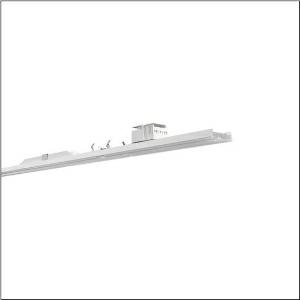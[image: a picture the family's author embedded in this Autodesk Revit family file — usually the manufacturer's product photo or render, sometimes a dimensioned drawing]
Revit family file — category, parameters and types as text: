
# Revit family: licross_r__11_recessed_mo_51tl19cn48xfd_8b6c
name_source: partatom
category: Lighting Fixtures
units: mm (PartAtom-declared; Revit-internal decimal feet)

## family parameters
Cut with Voids When Loaded = No
Host = Face
Light Source = No
Part Type = Normal
Room Calculation Point = No
Round Connector Dimension = Use Diameter
Shared = No

## types (1)
- --- (1 x LED, 3280 lm, 22.1 W, 4000K)
    Apparent Load = 22 VA
    CIE Flux Codes = 55 90 98 100 100
    Color Rendering = 80
    Color Temperature = 4000K
    Default Elevation = 1800 mm
    Description = Licross® 11 Recessed MOluminaire insert, length: 1.500mm, width: 66mm, height: 67mm, LED rated luminous flux: 8.020lm, light colour: 840, control gear: ON/OFF Multilumen, CLOi, control gear: ECG Multilumen, with plug, 6-pole, with phase selection, mains connection: 220..240V, AC/DC, 0/50..60Hz, without changeover relay, for emergency light function, for central battery installations according to DIN EN 60598-2-22, halogen-free wiring, primary light control with lens, of plastic, primary optical cover: cover, of PMMA, light emission: direct distribution, primary light characteristic: double asymmetric, protection rating (complete): IP40, insulation class (complete): insulation class I (protective earthing), certification: CE, ENEC, VDE, protection symbol: D if used in an environment without relevant dust loads with corresponding accessories, permissible ambient temperature for indoor applications: -35..+35°C, standard: EN 60598-2-22, reducing of maximum allowable ambient temperature of 5°C with ceiling mounting, corresponds to IFS (International Featured Standards) requirements for safety and quality in the food industry, packaging unit: 1 piece
    Height = 58 mm
    Lamp = 1 x LED
    Lamp Light Flux = 3280 lm
    Lamp Power = 22.1 W
    Lamp count = 1
    Length = 1500 mm
    Luminous efficacy = 148 lm/W
    Manufacturer = Siteco
    ModVariant = No
    Model = 51TL19CN48XFD
    Mounting Place = Ceiling
    Mounting Type = Pendant
    Number of Poles = 1
    OnlyDefault = Yes
    Power Factor = 1
    Product Name = Licross® 11 Recessed MO
    Product group = luminaire insert
    ProductGroupID = 902
    Protection Class = Protection class I
    Protection Degree = IP 40
    RLX_Detail_Level = 1
    RlxData = <blob elided: 20609 chars, md5=b694f6f2>
    Socket = socket
    Standby Power = 0 W
    System Light Flux = 3280 lm
    System Power = 22 W
    Type Comments = : DC mode (central or group accumulator) initial emergency light level
    Type Image = l_1266722.jpg
    URL = http://relux.com
    VarID = @adj_134467
    Voltage = 0 V
    Weight = 0.00 kg
    Width = 66 mm

## geometry (parser evidence)
native form markers: Blend x4, Sweep x10
no freeform markers — native parametric forms only
